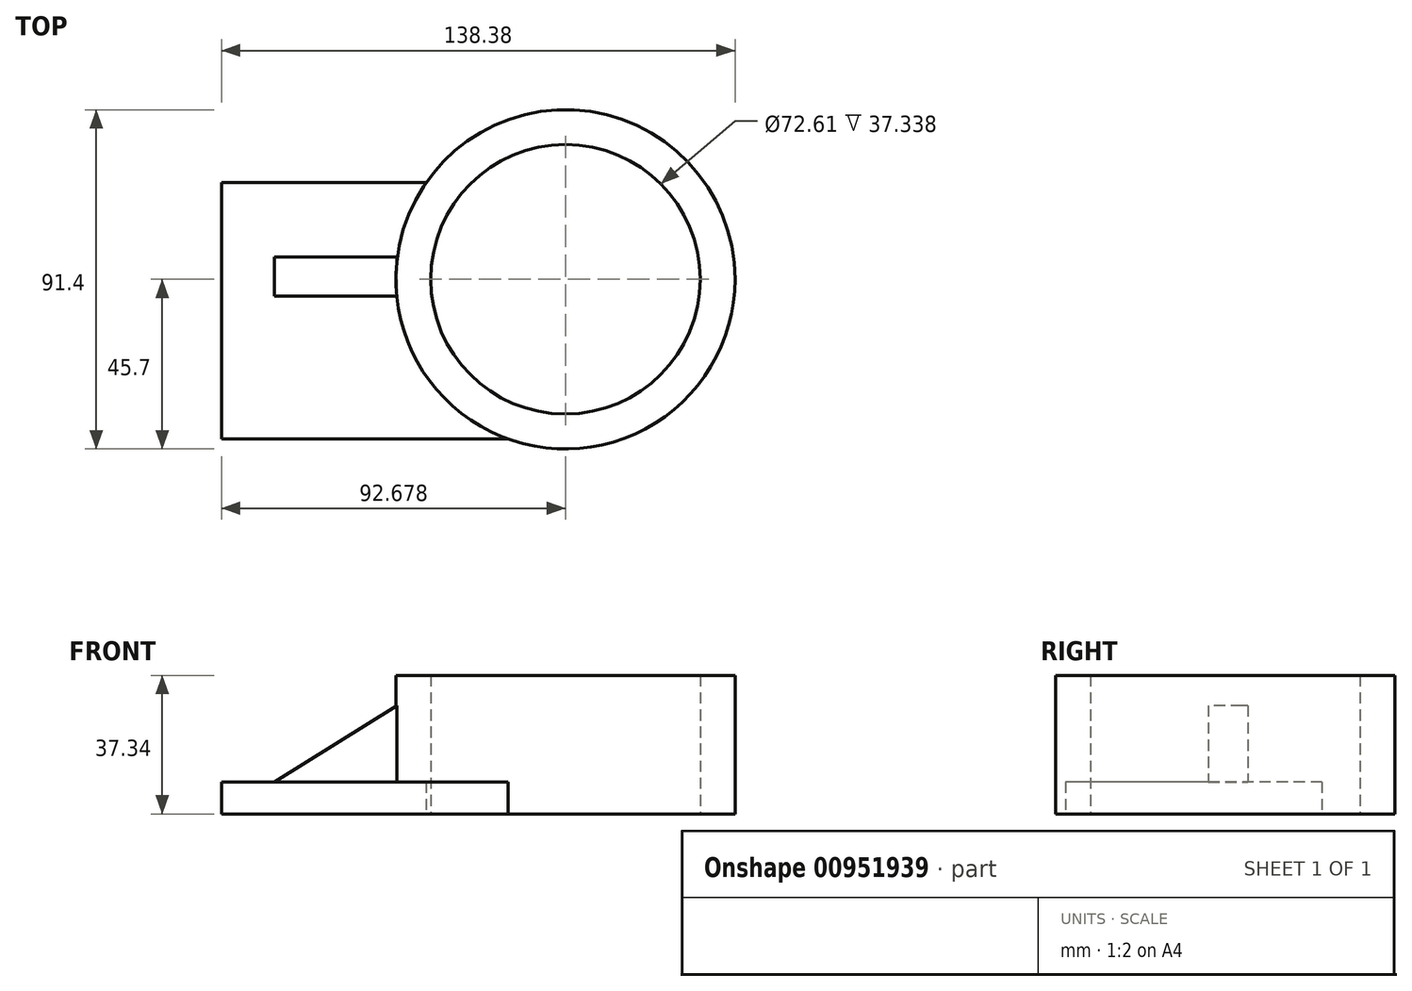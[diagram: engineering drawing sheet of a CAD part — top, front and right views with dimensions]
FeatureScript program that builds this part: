
annotation { "Feature Type Name" : "Feature", "Feature Type Description" : "" }
export const myFeature = defineFeature(function(context is Context, id is Id, definition is map)
    precondition{}
    {
        {
            var Q0;
            Q0=qCreatedBy(makeId("Top.planeOp"),FACE);
            var sketch = newSketch(context, id + "F0", { "sketchPlane" : qUnion([Q0])});
            skLineSegment(sketch, "E0.bottom", {"start": v(-65.48, 26.05) * mm, "end": v(-7.17, 26.05) * mm});
            skLineSegment(sketch, "E0.top", {"start": v(-65.48, -43.03) * mm, "end": v(12.9, -43.03) * mm});
            skLineSegment(sketch, "E0.left", {"start": v(-65.48, 26.05) * mm, "end": v(-65.48, -43.03) * mm});
            skCircle(sketch, "E1", {"center": v(32.1, 0) * mm, "radius": 47.12 * mm});
            skCircle(sketch, "E2", {"center": v(32.1, 0) * mm, "radius": 36.75 * mm});
            skSolve(sketch);
        }
        {
            var Q0;
            {var subQ0=sQuery(id+"F0.wireOp",EDGE,"E0.bottom");Q0=makeQuery(id+"F0.imprint","IMPRINT",FACE,{"disambiguationData":[TD([[makeQuery(id+"F0.imprint","IMPRINT",EDGE,{"derivedFrom":subQ0}),-1.0]])]});}
            extrude(context, id + "F1", {"entities" : qUnion([Q0]), "depth" : 8.64 * mm, "offsetDistance" : 25.4 * mm});
        }
        {
            var Q0;
            Q0=qCreatedBy(makeId("Top.planeOp"),FACE);
            var sketch = newSketch(context, id + "F2", { "sketchPlane" : qUnion([Q0])});
            skCircle(sketch, "E3", {"center": v(27.2, 0) * mm, "radius": 45.7 * mm});
            skCircle(sketch, "E4", {"center": v(27.2, 0) * mm, "radius": 36.3 * mm});
            skSolve(sketch);
        }
        {
            var Q0;
            Q0=makeQuery(id+"F2.imprint","IMPRINT",FACE,{"disambiguationData":[TD([[makeQuery(id+"F2.imprint","IMPRINT",EDGE,{"derivedFrom":sQuery(id+"F2.wireOp",EDGE,"E3")}),1.0]])]});
            extrude(context, id + "F3", {"entities" : qUnion([Q0]), "operationType" : NewBodyOperationType.ADD, "depth" : 37.34 * mm, "offsetDistance" : 25.4 * mm});
        }
        {
            var Q0;
            Q0=qCreatedBy(makeId("Top.planeOp"),FACE);
            var sketch = newSketch(context, id + "F4", { "sketchPlane" : qUnion([Q0])});
            skLineSegment(sketch, "E5.bottom", {"start": v(-12.55, 6.05) * mm, "end": v(-51.29, 6.05) * mm});
            skLineSegment(sketch, "E5.top", {"start": v(-12.55, -4.58) * mm, "end": v(-51.29, -4.58) * mm});
            skLineSegment(sketch, "E5.left", {"start": v(-12.55, 6.05) * mm, "end": v(-12.55, -4.58) * mm});
            skLineSegment(sketch, "E5.right", {"start": v(-51.29, 6.05) * mm, "end": v(-51.29, -4.58) * mm});
            skSolve(sketch);
        }
        {
            var Q0;
            Q0=makeQuery(id+"F4.imprint","IMPRINT",FACE,{"disambiguationData":[TD([[makeQuery(id+"F4.imprint","IMPRINT",EDGE,{"derivedFrom":sQuery(id+"F4.wireOp",EDGE,"E5.bottom")}),1.0]])]});
            extrude(context, id + "F5", {"entities" : qUnion([Q0]), "operationType" : NewBodyOperationType.ADD, "depth" : 29.2 * mm, "offsetDistance" : 25.4 * mm});
        }
        {
            var Q0;
            Q0=makeQuery(id+"F5.opExtrude","SWEPT_FACE",FACE,{"disambiguationData":[OSD([sQuery(id+"F4.wireOp",EDGE,"E5.top")])]});
            var sketch = newSketch(context, id + "F6", { "sketchPlane" : qUnion([Q0])});
            skLineSegment(sketch, "E6", {"start": v(-18.27, 29.21) * mm, "end": v(-51.29, 8.64) * mm});
            skSolve(sketch);
        }
        {
            var Q0;
            Q0=makeQuery(id+"F6.imprint","IMPRINT",FACE,{"disambiguationData":[TD([[makeQuery(id+"F6.imprint","IMPRINT",EDGE,{"derivedFrom":sQuery(id+"F6.wireOp",EDGE,"E6")}),-1.0]])]});
            extrude(context, id + "F7", {"entities" : qUnion([Q0]), "operationType" : NewBodyOperationType.REMOVE, "oppositeDirection" : true, "depth" : 25.4 * mm, "offsetDistance" : 25.4 * mm});
        }
    });
